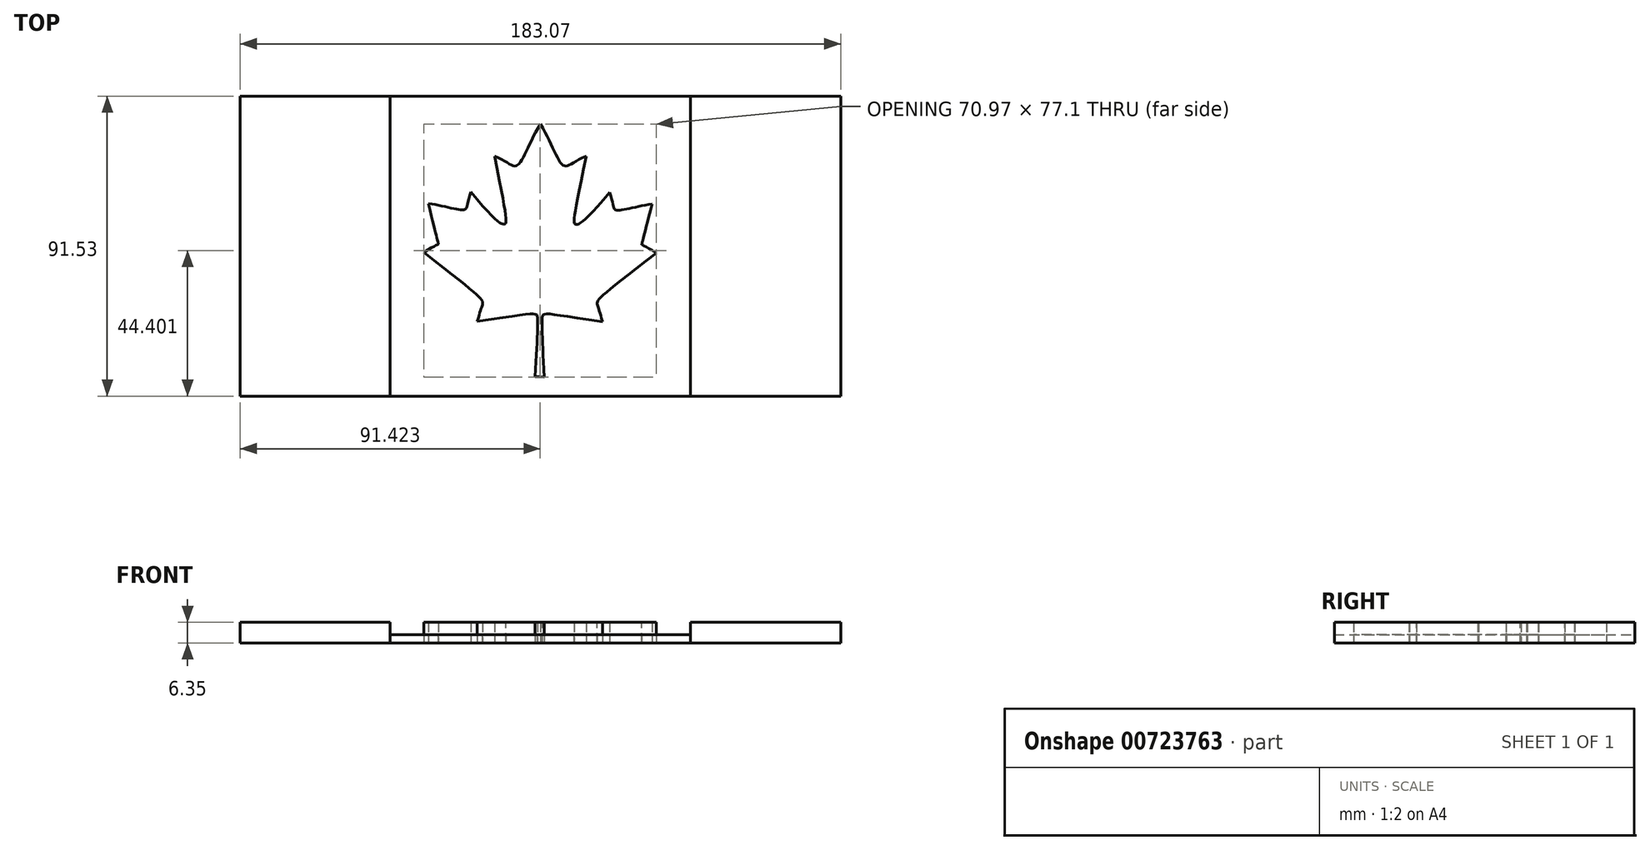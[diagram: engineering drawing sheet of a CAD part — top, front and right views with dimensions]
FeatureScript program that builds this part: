
annotation { "Feature Type Name" : "Feature", "Feature Type Description" : "" }
export const myFeature = defineFeature(function(context is Context, id is Id, definition is map)
    precondition{}
    {
        {
            var Q0;
            Q0=qCreatedBy(makeId("Top.planeOp"),FACE);
            var sketch = newSketch(context, id + "F0", { "sketchPlane" : qUnion([Q0])});
            skPoint(sketch, "E0.endSnap0", {"position": v(-1.12, 47.63) * mm});
            skLineSegment(sketch, "E1", {"start": v(-2.71, -38.04) * mm, "end": v(-1.33, -38.04) * mm});
            skLineSegment(sketch, "E2", {"start": v(-1.33, -38.04) * mm, "end": v(-1.12, 39.05) * mm});
            skLineSegment(sketch, "E3", {"start": v(-92.65, 47.63) * mm, "end": v(-92.65, -43.9) * mm});
            skLineSegment(sketch, "E4", {"start": v(90.42, -43.9) * mm, "end": v(-92.65, -43.9) * mm});
            skLineSegment(sketch, "E5", {"start": v(-92.65, 47.63) * mm, "end": v(90.42, 47.63) * mm});
            skLineSegment(sketch, "E6", {"start": v(90.42, 47.63) * mm, "end": v(90.42, -43.9) * mm});
            skLineSegment(sketch, "E7", {"start": v(-46.9, -43.9) * mm, "end": v(-46.9, 47.63) * mm});
            skLineSegment(sketch, "E8", {"start": v(44.65, -43.9) * mm, "end": v(44.65, 47.63) * mm});
            skFitSpline(sketch, "E9", {"points": [v(-22.34, 18.4) * mm, v(-12.12, 8.56) * mm, v(-15.1, 29.35) * mm], "startDerivative": vector(47.95, -58.33) * mm, "endDerivative": vector(-19.22, 98.37) * mm});
            skFitSpline(sketch, "E10", {"points": [v(-15.1, 29.35) * mm, v(-8.26, 26.5) * mm, v(-1.12, 39.05) * mm], "startDerivative": vector(28.13, -11.59) * mm, "endDerivative": vector(17.9, 27.44) * mm});
            skFitSpline(sketch, "E11", {"points": [v(-22.34, 18.4) * mm, v(-24.38, 13) * mm, v(-35.31, 14.9) * mm], "startDerivative": vector(-9.65, -28.7) * mm, "endDerivative": vector(-24.7, 3.67) * mm});
            skFitSpline(sketch, "E12", {"points": [v(-35.31, 14.9) * mm, v(-32.24, 2.65) * mm, v(-36.71, 0) * mm], "startDerivative": vector(12.55, -49.86) * mm, "endDerivative": vector(-34.35, -20.35) * mm});
            skFitSpline(sketch, "E13", {"points": [v(-36.71, 0) * mm, v(-18.89, -16.3) * mm, v(-20.34, -21.05) * mm], "startDerivative": vector(79.9, -62.52) * mm, "endDerivative": vector(-6.48, -25.44) * mm});
            skFitSpline(sketch, "E14", {"points": [v(-20.34, -21.05) * mm, v(-1.97, -20.27) * mm, v(-2.71, -38.04) * mm], "startDerivative": vector(105.14, 13.57) * mm, "endDerivative": vector(-3.03, -56.86) * mm});
            skFitSpline(sketch, "E15.MirrorCS", {"points": [v(12.8, 29.27) * mm, v(5.95, 26.46) * mm, v(-1.12, 39.05) * mm], "startDerivative": vector(-28.2, -11.43) * mm, "endDerivative": vector(-17.74, 27.54) * mm});
            skFitSpline(sketch, "E16.MirrorCS", {"points": [v(20, 18.28) * mm, v(9.71, 8.5) * mm, v(12.8, 29.27) * mm], "startDerivative": vector(-48.28, -58.05) * mm, "endDerivative": vector(19.77, 98.26) * mm});
            skFitSpline(sketch, "E17.MirrorCS", {"points": [v(20, 18.28) * mm, v(22, 12.87) * mm, v(32.94, 14.7) * mm], "startDerivative": vector(9.5, -28.75) * mm, "endDerivative": vector(24.71, 3.53) * mm});
            skFitSpline(sketch, "E18.MirrorCS", {"points": [v(32.94, 14.7) * mm, v(29.8, 2.48) * mm, v(34.26, -0.2) * mm], "startDerivative": vector(-12.83, -49.79) * mm, "endDerivative": vector(34.23, -20.55) * mm});
            skFitSpline(sketch, "E19.MirrorCS", {"points": [v(34.26, -0.2) * mm, v(16.34, -16.4) * mm, v(17.77, -21.16) * mm], "startDerivative": vector(-80.26, -62.06) * mm, "endDerivative": vector(6.34, -25.47) * mm});
            skFitSpline(sketch, "E20.MirrorCS", {"points": [v(17.77, -21.16) * mm, v(-0.6, -20.27) * mm, v(0.04, -38.05) * mm], "startDerivative": vector(-105.06, 14.16) * mm, "endDerivative": vector(2.7, -56.88) * mm});
            skLineSegment(sketch, "E21.MirrorCS", {"start": v(0.04, -38.05) * mm, "end": v(-1.33, -38.04) * mm});
            skLineSegment(sketch, "E22", {"start": v(-46.9, 47.63) * mm, "end": v(44.65, 47.63) * mm});
            skLineSegment(sketch, "E23", {"start": v(44.65, -43.9) * mm, "end": v(-46.9, -43.9) * mm});
            skLineSegment(sketch, "E24", {"start": v(-46.9, -43.9) * mm, "end": v(44.65, -43.9) * mm});
            skLineSegment(sketch, "E25", {"start": v(44.65, -43.27) * mm, "end": v(44.65, -43.9) * mm});
            skLineSegment(sketch, "E26", {"start": v(-46.9, -43.27) * mm, "end": v(-46.9, -43.9) * mm});
            skSolve(sketch);
        }
        {
            var Q0;
            Q0=makeQuery(id+"F0.imprint","IMPRINT",FACE,{"disambiguationData":[TD([[makeQuery(id+"F0.imprint","IMPRINT",EDGE,{"derivedFrom":sQuery(id+"F0.wireOp",EDGE,"E2")}),-1.0]])]});
            var Q1;
            Q1=makeQuery(id+"F0.imprint","IMPRINT",FACE,{"disambiguationData":[TD([[makeQuery(id+"F0.imprint","IMPRINT",EDGE,{"derivedFrom":sQuery(id+"F0.wireOp",EDGE,"E1")}),1.0]])]});
            extrude(context, id + "F1", {"entities" : qUnion([Q0, Q1]), "depth" : 6.35 * mm, "offsetDistance" : 25.4 * mm});
        }
        {
            var Q0;
            {var subQ0=sQuery(id+"F0.wireOp",EDGE,"E6");Q0=makeQuery(id+"F0.imprint","IMPRINT",FACE,{"disambiguationData":[TD([[makeQuery(id+"F0.imprint","IMPRINT",EDGE,{"derivedFrom":subQ0}),-1.0]])]});}
            var Q1;
            {var subQ0=sQuery(id+"F0.wireOp",EDGE,"E3");Q1=makeQuery(id+"F0.imprint","IMPRINT",FACE,{"disambiguationData":[TD([[makeQuery(id+"F0.imprint","IMPRINT",EDGE,{"derivedFrom":subQ0}),1.0]])]});}
            extrude(context, id + "F2", {"entities" : qUnion([Q0, Q1]), "depth" : 6.35 * mm, "offsetDistance" : 25.4 * mm});
        }
        {
            var Q0;
            Q0=makeQuery(id+"F0.imprint","IMPRINT",FACE,{"disambiguationData":[TD([[makeQuery(id+"F0.imprint","IMPRINT",EDGE,{"derivedFrom":sQuery(id+"F0.wireOp",EDGE,"E1")}),-1.0]])]});
            var Q1;
            Q1=sQuery(id+"F0.wireOp",EDGE,"E22");
            var Q2;
            Q2=sQuery(id+"F0.wireOp",EDGE,"E7");
            var Q3;
            Q3=sQuery(id+"F0.wireOp",EDGE,"E8");
            var Q4;
            Q4=sQuery(id+"F0.wireOp",EDGE,"E23");
            extrude(context, id + "F3", {"entities" : qUnion([Q0]), "surfaceEntities" : qUnion([Q1, Q2, Q3, Q4]), "depth" : 2.54 * mm, "offsetDistance" : 25.4 * mm});
        }
    });
